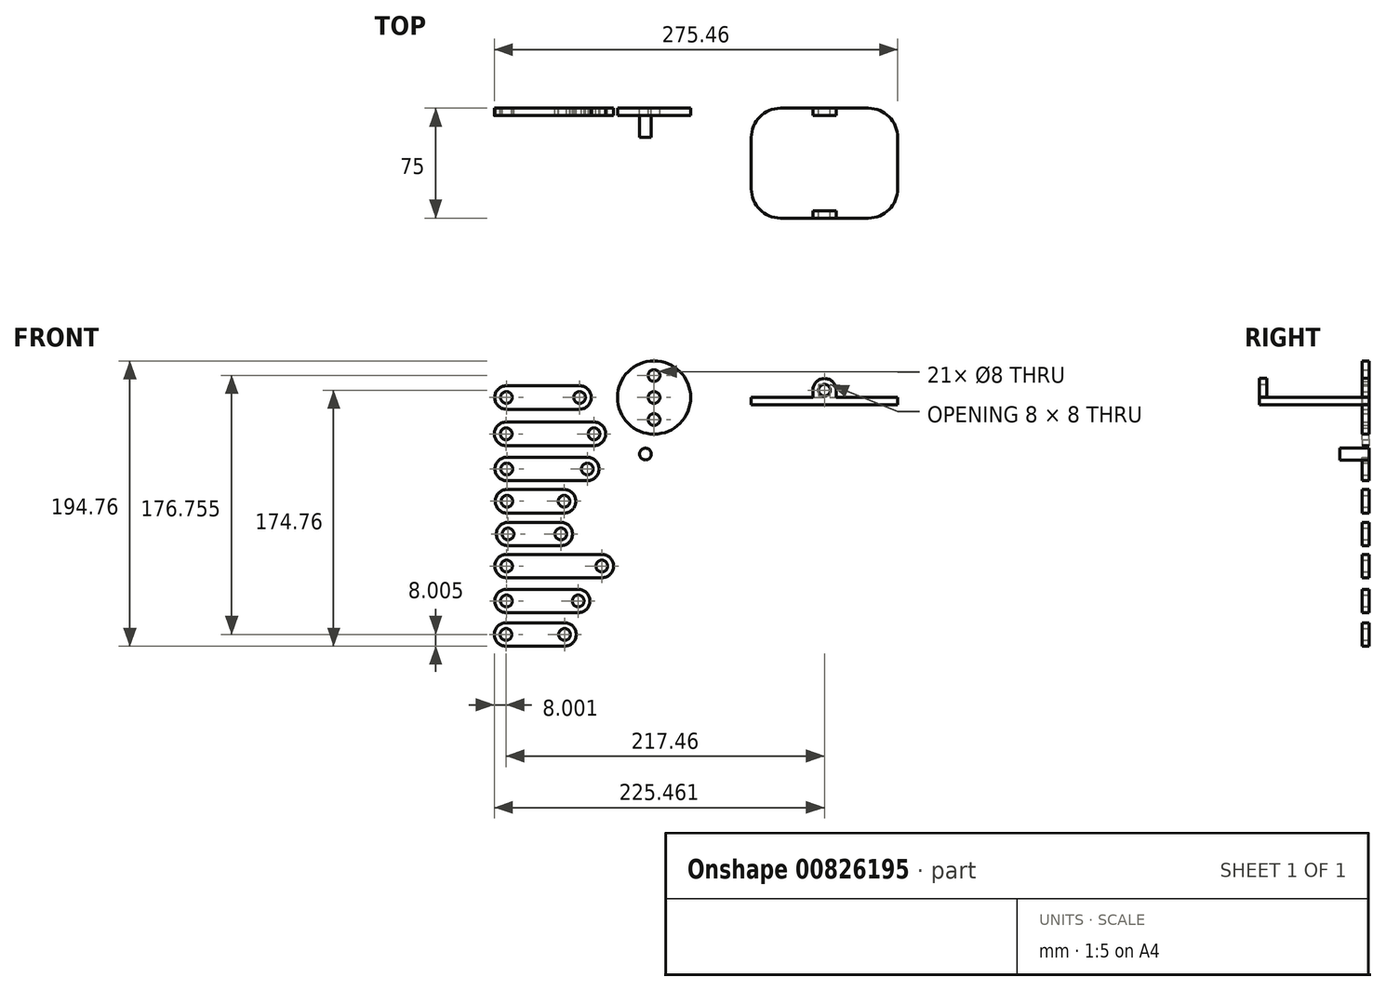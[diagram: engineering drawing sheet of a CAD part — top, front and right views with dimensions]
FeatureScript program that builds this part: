
annotation { "Feature Type Name" : "Feature", "Feature Type Description" : "" }
export const myFeature = defineFeature(function(context is Context, id is Id, definition is map)
    precondition{}
    {
        {
            assignVariable(context, id + "F0", {"name" : "thickness", "anyValue" : 5});
        }
        {
            var Q0;
            Q0=qCreatedBy(makeId("Front.planeOp"),FACE);
            var sketch = newSketch(context, id + "F1", { "sketchPlane" : qUnion([Q0])});
            skArc(sketch, "E0", {"start": v(0, 8) * mm, "mid": v(-8, 0) * mm, "end": v(0, -8) * mm});
            skArc(sketch, "E1", {"start": v(50, -8) * mm, "mid": v(58, 0) * mm, "end": v(50, 8) * mm});
            skLineSegment(sketch, "E2", {"start": v(0, 8) * mm, "end": v(50, 8) * mm});
            skLineSegment(sketch, "E3", {"start": v(0, -8) * mm, "end": v(50, -8) * mm});
            skCircle(sketch, "E4", {"center": v(0, 0) * mm, "radius": 4 * mm});
            skCircle(sketch, "E5", {"center": v(50, 0) * mm, "radius": 4 * mm});
            skSolve(sketch);
        }
        {
            var Q0;
            Q0=makeQuery(id+"F1.imprint","IMPRINT",FACE,{"disambiguationData":[TD([[makeQuery(id+"F1.imprint","IMPRINT",EDGE,{"derivedFrom":sQuery(id+"F1.wireOp",EDGE,"E0")}),1.0]])]});
            extrude(context, id + "F2", {"entities" : qUnion([Q0]), "depth" : (getVariable(context, 'thickness')) * mm, "offsetDistance" : 25 * mm});
        }
        {
            var Q0;
            Q0=qCreatedBy(makeId("Front.planeOp"),FACE);
            var sketch = newSketch(context, id + "F3", { "sketchPlane" : qUnion([Q0])});
            skArc(sketch, "E6", {"start": v(-0.14, -16.81) * mm, "mid": v(-8.14, -24.81) * mm, "end": v(-0.14, -32.81) * mm});
            skArc(sketch, "E7", {"start": v(59.86, -32.81) * mm, "mid": v(67.86, -24.81) * mm, "end": v(59.86, -16.81) * mm});
            skLineSegment(sketch, "E8", {"start": v(-0.14, -16.81) * mm, "end": v(59.86, -16.81) * mm});
            skLineSegment(sketch, "E9", {"start": v(-0.14, -32.81) * mm, "end": v(59.86, -32.81) * mm});
            skCircle(sketch, "E10", {"center": v(-0.14, -24.81) * mm, "radius": 4 * mm});
            skCircle(sketch, "E11", {"center": v(59.86, -24.81) * mm, "radius": 4 * mm});
            skSolve(sketch);
        }
        {
            var Q0;
            Q0=makeQuery(id+"F3.imprint","IMPRINT",FACE,{"disambiguationData":[TD([[makeQuery(id+"F3.imprint","IMPRINT",EDGE,{"derivedFrom":sQuery(id+"F3.wireOp",EDGE,"E6")}),1.0]])]});
            extrude(context, id + "F4", {"entities" : qUnion([Q0]), "depth" : (getVariable(context, 'thickness')) * mm, "offsetDistance" : 25 * mm});
        }
        {
            var Q0;
            Q0=qCreatedBy(makeId("Front.planeOp"),FACE);
            var sketch = newSketch(context, id + "F5", { "sketchPlane" : qUnion([Q0])});
            skArc(sketch, "E12", {"start": v(0.29, -40.8) * mm, "mid": v(-7.71, -48.8) * mm, "end": v(0.29, -56.8) * mm});
            skArc(sketch, "E13", {"start": v(55.29, -56.8) * mm, "mid": v(63.29, -48.8) * mm, "end": v(55.29, -40.8) * mm});
            skLineSegment(sketch, "E14", {"start": v(0.29, -40.8) * mm, "end": v(55.29, -40.8) * mm});
            skLineSegment(sketch, "E15", {"start": v(0.29, -56.8) * mm, "end": v(55.29, -56.8) * mm});
            skCircle(sketch, "E16", {"center": v(0.29, -48.8) * mm, "radius": 4 * mm});
            skCircle(sketch, "E17", {"center": v(55.29, -48.8) * mm, "radius": 4 * mm});
            skSolve(sketch);
        }
        {
            var Q0;
            Q0=makeQuery(id+"F5.imprint","IMPRINT",FACE,{"disambiguationData":[TD([[makeQuery(id+"F5.imprint","IMPRINT",EDGE,{"derivedFrom":sQuery(id+"F5.wireOp",EDGE,"E12")}),1.0]])]});
            extrude(context, id + "F6", {"entities" : qUnion([Q0]), "depth" : (getVariable(context, 'thickness')) * mm, "offsetDistance" : 25 * mm});
        }
        {
            var Q0;
            Q0=qCreatedBy(makeId("Front.planeOp"),FACE);
            var sketch = newSketch(context, id + "F7", { "sketchPlane" : qUnion([Q0])});
            skArc(sketch, "E18", {"start": v(0.4, -62.84) * mm, "mid": v(-7.6, -70.84) * mm, "end": v(0.4, -78.84) * mm});
            skArc(sketch, "E19", {"start": v(39.4, -78.84) * mm, "mid": v(47.4, -70.84) * mm, "end": v(39.4, -62.84) * mm});
            skLineSegment(sketch, "E20", {"start": v(0.4, -62.84) * mm, "end": v(39.4, -62.84) * mm});
            skLineSegment(sketch, "E21", {"start": v(0.4, -78.84) * mm, "end": v(39.4, -78.84) * mm});
            skCircle(sketch, "E22", {"center": v(0.4, -70.84) * mm, "radius": 4 * mm});
            skCircle(sketch, "E23", {"center": v(39.4, -70.84) * mm, "radius": 4 * mm});
            skSolve(sketch);
        }
        {
            var Q0;
            Q0=makeQuery(id+"F7.imprint","IMPRINT",FACE,{"disambiguationData":[TD([[makeQuery(id+"F7.imprint","IMPRINT",EDGE,{"derivedFrom":sQuery(id+"F7.wireOp",EDGE,"E18")}),1.0]])]});
            extrude(context, id + "F8", {"entities" : qUnion([Q0]), "depth" : (getVariable(context, 'thickness')) * mm, "offsetDistance" : 25 * mm});
        }
        {
            var Q0;
            Q0=qCreatedBy(makeId("Front.planeOp"),FACE);
            var sketch = newSketch(context, id + "F9", { "sketchPlane" : qUnion([Q0])});
            skArc(sketch, "E24", {"start": v(1.2, -85.15) * mm, "mid": v(-6.8, -93.15) * mm, "end": v(1.2, -101.15) * mm});
            skArc(sketch, "E25", {"start": v(37.2, -101.15) * mm, "mid": v(45.2, -93.15) * mm, "end": v(37.2, -85.15) * mm});
            skLineSegment(sketch, "E26", {"start": v(1.2, -85.15) * mm, "end": v(37.2, -85.15) * mm});
            skLineSegment(sketch, "E27", {"start": v(1.2, -101.15) * mm, "end": v(37.2, -101.15) * mm});
            skCircle(sketch, "E28", {"center": v(1.2, -93.15) * mm, "radius": 4 * mm});
            skCircle(sketch, "E29", {"center": v(37.2, -93.15) * mm, "radius": 4 * mm});
            skSolve(sketch);
        }
        {
            var Q0;
            Q0=makeQuery(id+"F9.imprint","IMPRINT",FACE,{"disambiguationData":[TD([[makeQuery(id+"F9.imprint","IMPRINT",EDGE,{"derivedFrom":sQuery(id+"F9.wireOp",EDGE,"E24")}),1.0]])]});
            extrude(context, id + "F10", {"entities" : qUnion([Q0]), "depth" : (getVariable(context, 'thickness')) * mm, "offsetDistance" : 25 * mm});
        }
        {
            var Q0;
            Q0=qCreatedBy(makeId("Front.planeOp"),FACE);
            var sketch = newSketch(context, id + "F11", { "sketchPlane" : qUnion([Q0])});
            skArc(sketch, "E30", {"start": v(0.17, -107.05) * mm, "mid": v(-7.83, -115.05) * mm, "end": v(0.17, -123.05) * mm});
            skArc(sketch, "E31", {"start": v(65.17, -123.05) * mm, "mid": v(73.17, -115.05) * mm, "end": v(65.17, -107.05) * mm});
            skLineSegment(sketch, "E32", {"start": v(0.17, -107.05) * mm, "end": v(65.17, -107.05) * mm});
            skLineSegment(sketch, "E33", {"start": v(0.17, -123.05) * mm, "end": v(65.17, -123.05) * mm});
            skCircle(sketch, "E34", {"center": v(0.17, -115.05) * mm, "radius": 4 * mm});
            skCircle(sketch, "E35", {"center": v(65.17, -115.05) * mm, "radius": 4 * mm});
            skSolve(sketch);
        }
        {
            var Q0;
            Q0=makeQuery(id+"F11.imprint","IMPRINT",FACE,{"disambiguationData":[TD([[makeQuery(id+"F11.imprint","IMPRINT",EDGE,{"derivedFrom":sQuery(id+"F11.wireOp",EDGE,"E30")}),1.0]])]});
            extrude(context, id + "F12", {"entities" : qUnion([Q0]), "depth" : (getVariable(context, 'thickness')) * mm, "offsetDistance" : 25 * mm});
        }
        {
            var Q0;
            Q0=qCreatedBy(makeId("Front.planeOp"),FACE);
            var sketch = newSketch(context, id + "F13", { "sketchPlane" : qUnion([Q0])});
            skArc(sketch, "E36", {"start": v(0.05, -130.88) * mm, "mid": v(-7.95, -138.88) * mm, "end": v(0.05, -146.88) * mm});
            skArc(sketch, "E37", {"start": v(49.05, -146.88) * mm, "mid": v(57.05, -138.88) * mm, "end": v(49.05, -130.88) * mm});
            skLineSegment(sketch, "E38", {"start": v(0.05, -130.88) * mm, "end": v(49.05, -130.88) * mm});
            skLineSegment(sketch, "E39", {"start": v(0.05, -146.88) * mm, "end": v(49.05, -146.88) * mm});
            skCircle(sketch, "E40", {"center": v(0.05, -138.88) * mm, "radius": 4 * mm});
            skCircle(sketch, "E41", {"center": v(49.05, -138.88) * mm, "radius": 4 * mm});
            skSolve(sketch);
        }
        {
            var Q0;
            Q0=makeQuery(id+"F13.imprint","IMPRINT",FACE,{"disambiguationData":[TD([[makeQuery(id+"F13.imprint","IMPRINT",EDGE,{"derivedFrom":sQuery(id+"F13.wireOp",EDGE,"E36")}),1.0]])]});
            extrude(context, id + "F14", {"entities" : qUnion([Q0]), "depth" : (getVariable(context, 'thickness')) * mm, "offsetDistance" : 25 * mm});
        }
        {
            var Q0;
            Q0=qCreatedBy(makeId("Front.planeOp"),FACE);
            var sketch = newSketch(context, id + "F15", { "sketchPlane" : qUnion([Q0])});
            skCircle(sketch, "E42", {"center": v(100.84, 0) * mm, "radius": 25 * mm});
            skCircle(sketch, "E43", {"center": v(100.84, 0) * mm, "radius": 15 * mm, "construction": true});
            skLineSegment(sketch, "E44", {"start": v(100.84, 0) * mm, "end": v(100.84, 15) * mm, "construction": true});
            skLineSegment(sketch, "E45", {"start": v(100.84, 0) * mm, "end": v(100.84, -15) * mm, "construction": true});
            skCircle(sketch, "E46", {"center": v(100.84, 15) * mm, "radius": 4 * mm});
            skCircle(sketch, "E47", {"center": v(100.84, -15) * mm, "radius": 4 * mm});
            skCircle(sketch, "E48", {"center": v(100.84, 0) * mm, "radius": 4 * mm});
            skSolve(sketch);
        }
        {
            var Q0;
            Q0=makeQuery(id+"F15.imprint","IMPRINT",FACE,{"disambiguationData":[TD([[makeQuery(id+"F15.imprint","IMPRINT",EDGE,{"derivedFrom":sQuery(id+"F15.wireOp",EDGE,"E42")}),1.0]])]});
            extrude(context, id + "F16", {"entities" : qUnion([Q0]), "depth" : (getVariable(context, 'thickness')) * mm, "offsetDistance" : 25 * mm});
        }
        {
            var Q0;
            Q0=qCreatedBy(makeId("Front.planeOp"),FACE);
            var sketch = newSketch(context, id + "F17", { "sketchPlane" : qUnion([Q0])});
            skLineSegment(sketch, "E49.top", {"start": v(167.21, -5) * mm, "end": v(267.21, -5) * mm});
            skLineSegment(sketch, "E49.left", {"start": v(267.21, 0) * mm, "end": v(267.21, -5) * mm});
            skLineSegment(sketch, "E49.right", {"start": v(167.21, 0) * mm, "end": v(167.21, -5) * mm});
            skArc(sketch, "E50", {"start": v(225.21, 5) * mm, "mid": v(217.21, 13) * mm, "end": v(209.21, 5) * mm});
            skLineSegment(sketch, "E51", {"start": v(209.21, 5) * mm, "end": v(209.21, 0) * mm});
            skLineSegment(sketch, "E52", {"start": v(225.21, 5) * mm, "end": v(225.21, 0) * mm});
            skCircle(sketch, "E53", {"center": v(217.21, 5) * mm, "radius": 4 * mm});
            skLineSegment(sketch, "E54.trimOffspring", {"start": v(167.21, 0) * mm, "end": v(209.21, 0) * mm});
            skLineSegment(sketch, "E55.trimOffspring", {"start": v(225.21, 0) * mm, "end": v(267.21, 0) * mm});
            skSolve(sketch);
        }
        {
            var Q0;
            Q0=makeQuery(id+"F17.imprint","IMPRINT",FACE,{"disambiguationData":[TD([[makeQuery(id+"F17.imprint","IMPRINT",EDGE,{"derivedFrom":sQuery(id+"F17.wireOp",EDGE,"E49.top")}),1.0]])]});
            extrude(context, id + "F18", {"entities" : qUnion([Q0]), "depth" : 75 * mm, "offsetDistance" : 25 * mm});
        }
        {
            var Q0;
            Q0=makeQuery(id+"F18.opExtrude","SWEPT_FACE",FACE,{"disambiguationData":[OSD([sQuery(id+"F17.wireOp",EDGE,"E49.left")])]});
            var sketch = newSketch(context, id + "F19", { "sketchPlane" : qUnion([Q0])});
            skLineSegment(sketch, "E56.bottom", {"start": v(-70, 0) * mm, "end": v(-5, 0) * mm});
            skLineSegment(sketch, "E56.top", {"start": v(-70, 14.12) * mm, "end": v(-5, 14.12) * mm});
            skLineSegment(sketch, "E56.left", {"start": v(-70, 0) * mm, "end": v(-70, 14.12) * mm});
            skLineSegment(sketch, "E56.right", {"start": v(-5, 0) * mm, "end": v(-5, 14.12) * mm});
            skSolve(sketch);
        }
        {
            var Q0;
            Q0=makeQuery(id+"F19.imprint","IMPRINT",FACE,{"disambiguationData":[TD([[makeQuery(id+"F19.imprint","IMPRINT",EDGE,{"derivedFrom":sQuery(id+"F19.wireOp",EDGE,"E56.bottom")}),1.0]])]});
            extrude(context, id + "F20", {"entities" : qUnion([Q0]), "operationType" : NewBodyOperationType.REMOVE, "endBound" : BoundingType.THROUGH_ALL, "oppositeDirection" : true, "depth" : 25 * mm, "offsetDistance" : 25 * mm});
        }
        {
            var Q0;
            Q0=makeQuery(id+"F18.opExtrude","CAP_EDGE",EDGE,{"disambiguationData":[OSD([sQuery(id+"F17.wireOp",EDGE,"E49.left")])],"isStart":false});
            var Q1;
            Q1=makeQuery(id+"F18.opExtrude","CAP_EDGE",EDGE,{"disambiguationData":[OSD([sQuery(id+"F17.wireOp",EDGE,"E49.left")])],"isStart":true});
            var Q2;
            Q2=makeQuery(id+"F18.opExtrude","CAP_EDGE",EDGE,{"disambiguationData":[OSD([sQuery(id+"F17.wireOp",EDGE,"E49.right")])],"isStart":true});
            var Q3;
            Q3=makeQuery(id+"F18.opExtrude","CAP_EDGE",EDGE,{"disambiguationData":[OSD([sQuery(id+"F17.wireOp",EDGE,"E49.right")])],"isStart":false});
            fillet(context, id + "F21", {"entities" : qUnion([Q0, Q1, Q2, Q3]), "radius" : 20 * mm, "tangentPropagation" : true, "allowEdgeOverflow" : false});
        }
        {
            var Q0;
            Q0=qCreatedBy(makeId("Front.planeOp"),FACE);
            var sketch = newSketch(context, id + "F22", { "sketchPlane" : qUnion([Q0])});
            skArc(sketch, "E57", {"start": v(-0.25, -153.76) * mm, "mid": v(-8.25, -161.76) * mm, "end": v(-0.25, -169.76) * mm});
            skArc(sketch, "E58", {"start": v(39.75, -169.76) * mm, "mid": v(47.75, -161.76) * mm, "end": v(39.75, -153.76) * mm});
            skLineSegment(sketch, "E59", {"start": v(-0.25, -153.76) * mm, "end": v(39.75, -153.76) * mm});
            skLineSegment(sketch, "E60", {"start": v(-0.25, -169.76) * mm, "end": v(39.75, -169.76) * mm});
            skCircle(sketch, "E61", {"center": v(-0.25, -161.76) * mm, "radius": 4 * mm});
            skCircle(sketch, "E62", {"center": v(39.75, -161.76) * mm, "radius": 4 * mm});
            skSolve(sketch);
        }
        {
            var Q0;
            Q0=makeQuery(id+"F22.imprint","IMPRINT",FACE,{"disambiguationData":[TD([[makeQuery(id+"F22.imprint","IMPRINT",EDGE,{"derivedFrom":sQuery(id+"F22.wireOp",EDGE,"E57")}),1.0]])]});
            extrude(context, id + "F23", {"entities" : qUnion([Q0]), "depth" : (getVariable(context, 'thickness')) * mm, "offsetDistance" : 25 * mm});
        }
        {
            var Q0;
            Q0=qCreatedBy(makeId("Front.planeOp"),FACE);
            var sketch = newSketch(context, id + "F24", { "sketchPlane" : qUnion([Q0])});
            skCircle(sketch, "E63", {"center": v(94.95, -38.6) * mm, "radius": 4 * mm});
            skSolve(sketch);
        }
        {
            var Q0;
            Q0=makeQuery(id+"F24.imprint","IMPRINT",FACE,{"disambiguationData":[TD([[makeQuery(id+"F24.imprint","IMPRINT",EDGE,{"derivedFrom":sQuery(id+"F24.wireOp",EDGE,"E63")}),1.0]])]});
            extrude(context, id + "F25", {"entities" : qUnion([Q0]), "depth" : 20 * mm, "offsetDistance" : 25 * mm});
        }
    });
